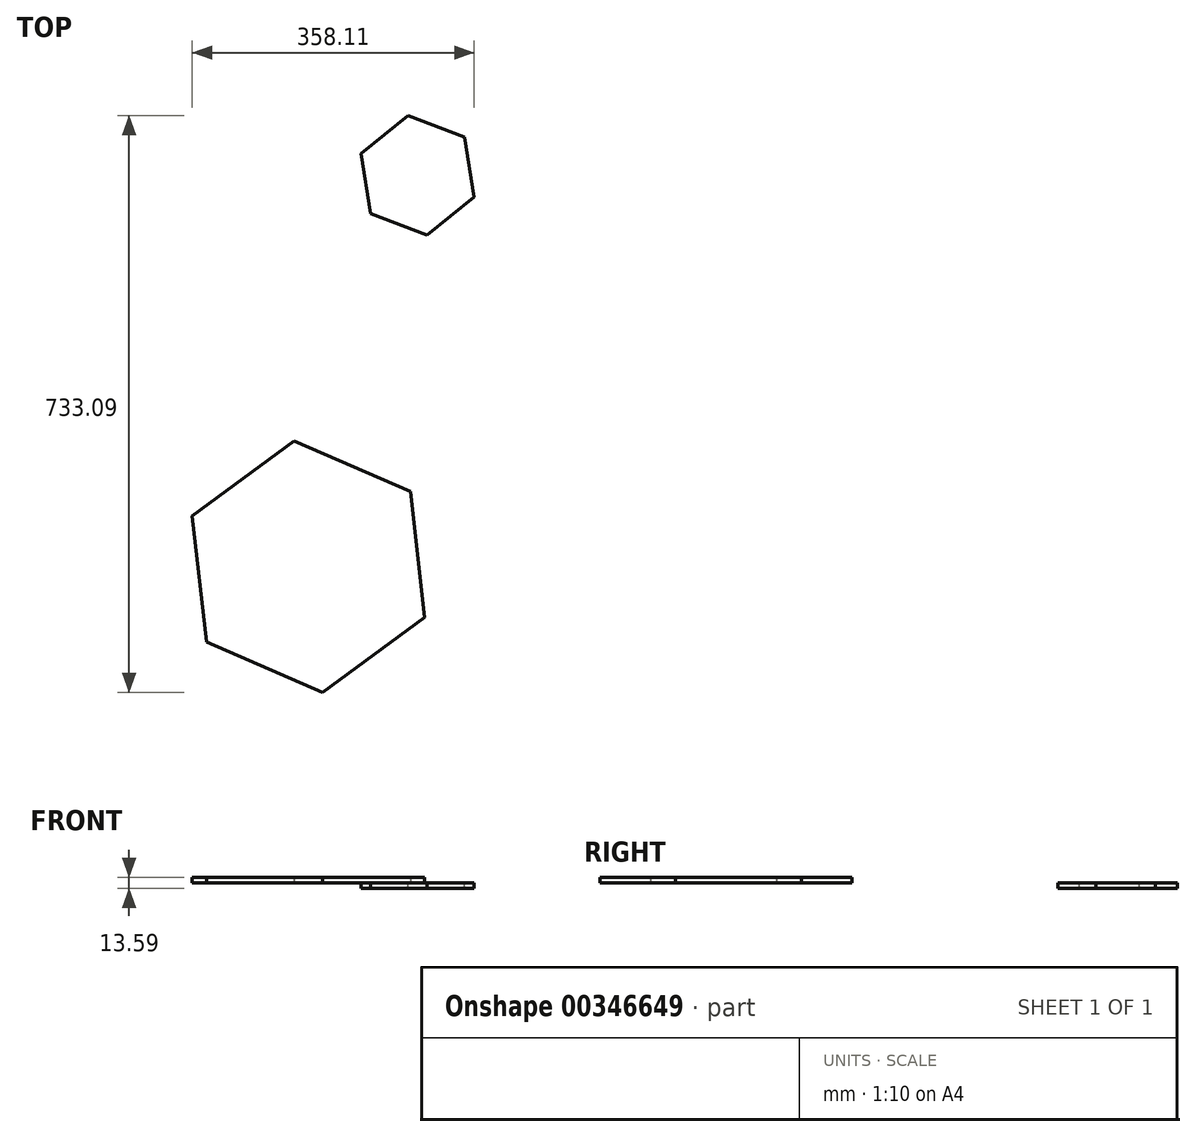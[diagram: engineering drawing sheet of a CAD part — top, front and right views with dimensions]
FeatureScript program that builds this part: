
annotation { "Feature Type Name" : "Feature", "Feature Type Description" : "" }
export const myFeature = defineFeature(function(context is Context, id is Id, definition is map)
    precondition{}
    {
        {
            var Q0;
            Q0=qCreatedBy(makeId("Top.planeOp"),FACE);
            var sketch = newSketch(context, id + "F0", { "sketchPlane" : qUnion([Q0])});
            skCircle(sketch, "E0.cCircle", {"center": v(-15.32, 19.9) * mm, "radius": 76.85 * mm, "construction": true});
            skLineSegment(sketch, "E0.0", {"start": v(56.41, -7.67) * mm, "end": v(-3.33, -56.01) * mm});
            skLineSegment(sketch, "E0.1", {"start": v(-3.33, -56.01) * mm, "end": v(-75.07, -28.44) * mm});
            skLineSegment(sketch, "E0.2", {"start": v(-75.07, -28.44) * mm, "end": v(-87.06, 47.47) * mm});
            skLineSegment(sketch, "E0.3", {"start": v(-87.06, 47.47) * mm, "end": v(-27.3, 95.81) * mm});
            skLineSegment(sketch, "E0.4", {"start": v(-27.3, 95.81) * mm, "end": v(44.43, 68.24) * mm});
            skLineSegment(sketch, "E0.5", {"start": v(44.43, 68.24) * mm, "end": v(56.41, -7.67) * mm});
            skSolve(sketch);
        }
        {
            var Q0;
            Q0=makeQuery(id+"F0.imprint","IMPRINT",FACE,{"disambiguationData":[TD([[makeQuery(id+"F0.imprint","IMPRINT",EDGE,{"derivedFrom":sQuery(id+"F0.wireOp",EDGE,"E0.0")}),-1.0]])]});
            var sketch = newSketch(context, id + "F1", { "sketchPlane" : qUnion([Q0])});
            skSolve(sketch);
        }
        {
            var Q0;
            Q0=makeQuery(id+"F1.imprint","IMPRINT",FACE,{"disambiguationData":[TD([[makeQuery(id+"F1.imprint","IMPRINT",EDGE,{"derivedFrom":makeQuery(id+"F0.imprint","IMPRINT",EDGE,{"derivedFrom":sQuery(id+"F0.wireOp",EDGE,"E0.0")})}),-1.0]])]});
            extrude(context, id + "F2", {"entities" : qUnion([Q0]), "oppositeDirection" : true, "depth" : 6.94 * mm});
        }
        {
            var Q0;
            Q0=qCreatedBy(makeId("Top.planeOp"),FACE);
            var sketch = newSketch(context, id + "F3", { "sketchPlane" : qUnion([Q0])});
            skCircle(sketch, "E1.cCircle", {"center": v(-154.05, -477.3) * mm, "radius": 161 * mm, "construction": true});
            skLineSegment(sketch, "E1.0", {"start": v(-6.41, -541.52) * mm, "end": v(-135.84, -637.28) * mm});
            skLineSegment(sketch, "E1.1", {"start": v(-135.84, -637.28) * mm, "end": v(-283.49, -573.07) * mm});
            skLineSegment(sketch, "E1.2", {"start": v(-283.49, -573.07) * mm, "end": v(-301.7, -413.1) * mm});
            skLineSegment(sketch, "E1.3", {"start": v(-301.7, -413.1) * mm, "end": v(-172.26, -317.34) * mm});
            skLineSegment(sketch, "E1.4", {"start": v(-172.26, -317.34) * mm, "end": v(-24.62, -381.55) * mm});
            skLineSegment(sketch, "E1.5", {"start": v(-24.62, -381.55) * mm, "end": v(-6.41, -541.52) * mm});
            skSolve(sketch);
        }
        {
            var Q0;
            Q0 = qSketchRegion(id + "F3", true);
            extrude(context, id + "F4", {"entities" : qUnion([Q0]), "depth" : 6.65 * mm});
        }
    });
